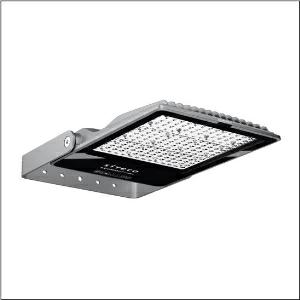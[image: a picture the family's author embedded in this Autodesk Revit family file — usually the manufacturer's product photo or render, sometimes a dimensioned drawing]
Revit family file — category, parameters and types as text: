
# Revit family: sicompact_r__31_midi___pl32_5xa7581e2k23_2195
name_source: partatom
category: Lighting Fixtures
units: mm (PartAtom-declared; Revit-internal decimal feet)

## family parameters
Cut with Voids When Loaded = No
Host = Face
Light Source = No
Part Type = Normal
Room Calculation Point = No
Round Connector Dimension = Use Diameter
Shared = No

## types (1)
- SiCompact® 31 midi  PL32 (1 x LED, 37000 lm, 243 W, 4000K)
    Apparent Load = 243 VA
    CIE Flux Codes = 32 69 98 100 100
    Color Rendering = 70
    Color Temperature = 4000K
    Default Elevation = 1800 mm
    Description = SiCompact® 31 midi, floodlight, primary light control with lens, of plastic, of toughened safety glass, transparent, light distribution: PL32, light emission: direct distribution, primary light characteristic: asymmetric, installation type: surface-mounted, LED, High Power LED, rated luminous flux: 37.000lm, luminous efficacy: 152lm/W, light colour: 740, colour temperature: 4000K, control gear: ECG, with cable, 3x 1.5mm², mains connection: 220..240V, AC, 50/60Hz, connection cable pre-assembled, cable length: 2m, rated input power: 243W, of diecast aluminium, specular, metallic grey (RAL 9006), length: 560mm, width: 330mm, height: 62mm, bracket, of sheet steel, coated, metallic grey (RAL 9006), ON/OFF, protection rating (complete): IP66, insulation class (complete): insulation class I (protective earthing), certification: CE, ENEC, impact resistance: IK08, permissible operating ambient temperature: -40..+45°C, packaging unit: 1 piece

Light Distribution: PL32
    Height = 62 mm  [stored 0.203412 ft]
    Lamp = 1 x LED
    Lamp Light Flux = 37000 lm
    Lamp Power = 243 W
    Lamp count = 1
    Length = 560 mm
    Luminous efficacy = 152 lm/W
    Manufacturer = Siteco
    ModVariant = No
    Model = 5XA7581E2K23
    Mounting Place = Wall
    Mounting Type = Surface mounted
    Number of Poles = 1
    OnlyDefault = Yes
    Power Factor = 1
    Product Name = SiCompact® 31 midi | PL32
    Product group = floodlight | wall mounted
    ProductGroupID = 2001
    Protection Class = Protection class I
    Protection Degree = IP 66
    RLX_Detail_Level = 1
    RLX_Emergency_Light_Flux = 0 lm
    RLX_Emergency_Type = 0
    RLX_Emergency_Type_DB = No
    RlxData = <blob elided: 98225 chars, md5=b3b2dd7a>
    Socket = socket
    Standby Power = 0 W
    System Light Flux = 37000 lm
    System Power = 243 W
    Type Comments = Product without accessories
    Type Image = l_1006415.jpg
    URL = http://relux.com
    VarID = ---
    Voltage = 0 V
    Weight = 0.00 kg
    Width = 333 mm

note: [stored X ft] marks values corroborated as IEEE doubles in the binary element streams (Revit-internal decimal feet)

## geometry (parser evidence)
native form markers: Blend x4, Sweep x12
no freeform markers — native parametric forms only
